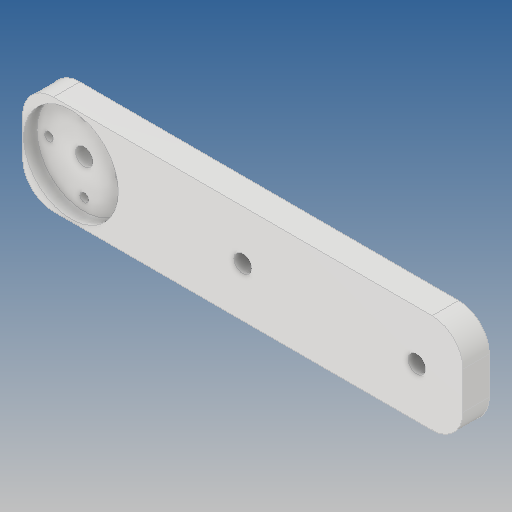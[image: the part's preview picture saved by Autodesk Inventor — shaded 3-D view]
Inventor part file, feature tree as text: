
AUTODESK INVENTOR PART (.ipt)
format: ipt  version: 2020 (Build 240168000, 168)  size: 145,408 bytes
history: native  units: mm
features: extrude x4, sketch x4, other x1, fillet x1
ambient origin geometry x8: Origin, YZ Plane, XZ Plane, XY Plane, X Axis, Y Axis, Z Axis, Center Point
bodies: Body1 (feature_tree)
feature tree (10):
  other  "Твердое тело1"
  extrude  "Выдавливание1"  Depth=100.0mm
  extrude  "Выдавливание2"  Depth=22.5mm
  extrude  "Выдавливание3"  Depth=10.5mm
  fillet  "Сопряжение1"  Radius=11.0mm
  extrude  "Выдавливание4"  Depth=21.0mm
  sketch  "Эскиз1"
  sketch  "Эскиз2"
  sketch  "Эскиз3"
  sketch  "Эскиз4"
